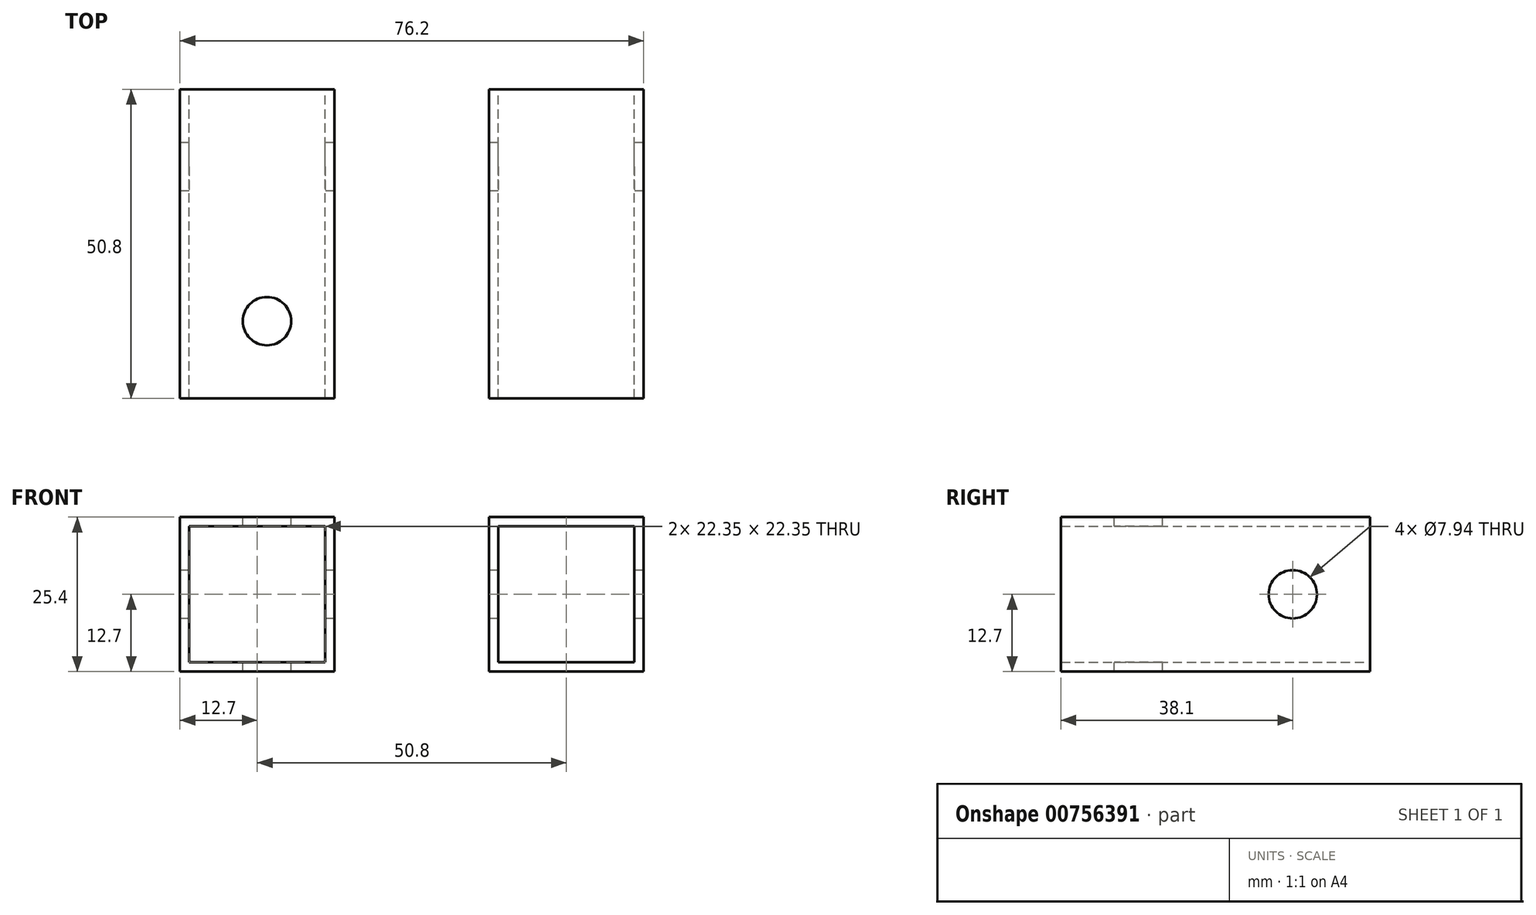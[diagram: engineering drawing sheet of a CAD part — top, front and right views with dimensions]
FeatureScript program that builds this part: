
annotation { "Feature Type Name" : "Feature", "Feature Type Description" : "" }
export const myFeature = defineFeature(function(context is Context, id is Id, definition is map)
    precondition{}
    {
        {
            var Q0;
            Q0=qCreatedBy(makeId("Front.planeOp"),FACE);
            var sketch = newSketch(context, id + "F0", { "sketchPlane" : qUnion([Q0])});
            skLineSegment(sketch, "E0.bottom", {"start": v(1.52, 23.88) * mm, "end": v(23.88, 23.88) * mm});
            skLineSegment(sketch, "E0.top", {"start": v(1.52, 1.52) * mm, "end": v(23.88, 1.52) * mm});
            skLineSegment(sketch, "E0.left", {"start": v(1.52, 23.88) * mm, "end": v(1.52, 1.52) * mm});
            skLineSegment(sketch, "E0.right", {"start": v(23.88, 23.88) * mm, "end": v(23.88, 1.52) * mm});
            skLineSegment(sketch, "E1.bottom", {"start": v(0, 0) * mm, "end": v(25.4, 0) * mm});
            skLineSegment(sketch, "E1.top", {"start": v(0, 25.4) * mm, "end": v(25.4, 25.4) * mm});
            skLineSegment(sketch, "E1.left", {"start": v(0, 0) * mm, "end": v(0, 25.4) * mm});
            skLineSegment(sketch, "E1.right", {"start": v(25.4, 0) * mm, "end": v(25.4, 25.4) * mm});
            skLineSegment(sketch, "E2.bottom", {"start": v(52.32, 23.88) * mm, "end": v(74.68, 23.88) * mm});
            skLineSegment(sketch, "E2.top", {"start": v(52.32, 1.52) * mm, "end": v(74.68, 1.52) * mm});
            skLineSegment(sketch, "E2.left", {"start": v(52.32, 23.88) * mm, "end": v(52.32, 1.52) * mm});
            skLineSegment(sketch, "E2.right", {"start": v(74.68, 23.88) * mm, "end": v(74.68, 1.52) * mm});
            skLineSegment(sketch, "E3.bottom", {"start": v(50.8, 0) * mm, "end": v(76.2, 0) * mm});
            skLineSegment(sketch, "E3.top", {"start": v(50.8, 25.4) * mm, "end": v(76.2, 25.4) * mm});
            skLineSegment(sketch, "E3.left", {"start": v(50.8, 0) * mm, "end": v(50.8, 25.4) * mm});
            skLineSegment(sketch, "E3.right", {"start": v(76.2, 0) * mm, "end": v(76.2, 25.4) * mm});
            skSolve(sketch);
        }
        {
            var Q0;
            Q0=makeQuery(id+"F0.imprint","IMPRINT",FACE,{"disambiguationData":[TD([[makeQuery(id+"F0.imprint","IMPRINT",EDGE,{"derivedFrom":sQuery(id+"F0.wireOp",EDGE,"E0.bottom")}),1.0]])]});
            var Q1;
            Q1=makeQuery(id+"F0.imprint","IMPRINT",FACE,{"disambiguationData":[TD([[makeQuery(id+"F0.imprint","IMPRINT",EDGE,{"derivedFrom":sQuery(id+"F0.wireOp",EDGE,"E2.bottom")}),1.0]])]});
            extrude(context, id + "F1", {"entities" : qUnion([Q0, Q1]), "depth" : 50.8 * mm, "offsetDistance" : 25.4 * mm});
        }
        {
            var Q0;
            Q0=makeQuery(id+"F1.opExtrude","SWEPT_FACE",FACE,{"disambiguationData":[OSD([sQuery(id+"F0.wireOp",EDGE,"E1.top")])]});
            var sketch = newSketch(context, id + "F2", { "sketchPlane" : qUnion([Q0])});
            skLineSegment(sketch, "E4", {"start": v(14.29, -50.8) * mm, "end": v(14.29, -25.4) * mm, "construction": true});
            skLineSegment(sketch, "E5", {"start": v(25.4, -25.4) * mm, "end": v(0, -25.4) * mm, "construction": true});
            skCircle(sketch, "E6", {"center": v(14.29, -38.1) * mm, "radius": 3.97 * mm});
            skPoint(sketch, "E7.0", {"position": v(50.8, 0) * mm});
            skPoint(sketch, "E8.0", {"position": v(25.4, 0) * mm});
            skLineSegment(sketch, "E9", {"start": v(25.4, 0) * mm, "end": v(50.8, 0) * mm, "construction": true});
            skLineSegment(sketch, "E10", {"start": v(38.1, 0) * mm, "end": v(38.1, -50.8) * mm, "construction": true});
            skCircle(sketch, "E11.MirrorC", {"center": v(61.91, -38.1) * mm, "radius": 3.97 * mm});
            skSolve(sketch);
        }
        {
            var Q0;
            Q0=makeQuery(id+"F2.imprint","IMPRINT",FACE,{"disambiguationData":[TD([[makeQuery(id+"F2.imprint","IMPRINT",EDGE,{"derivedFrom":sQuery(id+"F2.wireOp",EDGE,"E6")}),1.0]])]});
            var Q1;
            Q1=makeQuery(id+"F2.imprint","IMPRINT",FACE,{"disambiguationData":[TD([[makeQuery(id+"F2.imprint","IMPRINT",EDGE,{"derivedFrom":sQuery(id+"F2.wireOp",EDGE,"E11.MirrorC")}),-1.0]])]});
            extrude(context, id + "F3", {"entities" : qUnion([Q0, Q1]), "operationType" : NewBodyOperationType.REMOVE, "endBound" : BoundingType.THROUGH_ALL, "oppositeDirection" : true, "depth" : 25.4 * mm, "offsetDistance" : 25.4 * mm});
        }
        {
            var Q0;
            Q0=makeQuery(id+"F1.opExtrude","SWEPT_FACE",FACE,{"disambiguationData":[OSD([sQuery(id+"F0.wireOp",EDGE,"E1.left")])]});
            var sketch = newSketch(context, id + "F4", { "sketchPlane" : qUnion([Q0])});
            skLineSegment(sketch, "E12", {"start": v(25.4, 25.4) * mm, "end": v(25.4, 0) * mm, "construction": true});
            skLineSegment(sketch, "E13", {"start": v(25.4, 12.7) * mm, "end": v(12.7, 12.7) * mm, "construction": true});
            skCircle(sketch, "E14", {"center": v(12.7, 12.7) * mm, "radius": 3.97 * mm});
            skSolve(sketch);
        }
        {
            var Q0;
            Q0=makeQuery(id+"F4.imprint","IMPRINT",FACE,{"disambiguationData":[TD([[makeQuery(id+"F4.imprint","IMPRINT",EDGE,{"derivedFrom":sQuery(id+"F4.wireOp",EDGE,"E14")}),1.0]])]});
            extrude(context, id + "F5", {"entities" : qUnion([Q0]), "operationType" : NewBodyOperationType.REMOVE, "endBound" : BoundingType.THROUGH_ALL, "oppositeDirection" : true, "depth" : 25.4 * mm, "offsetDistance" : 25.4 * mm});
        }
    });
